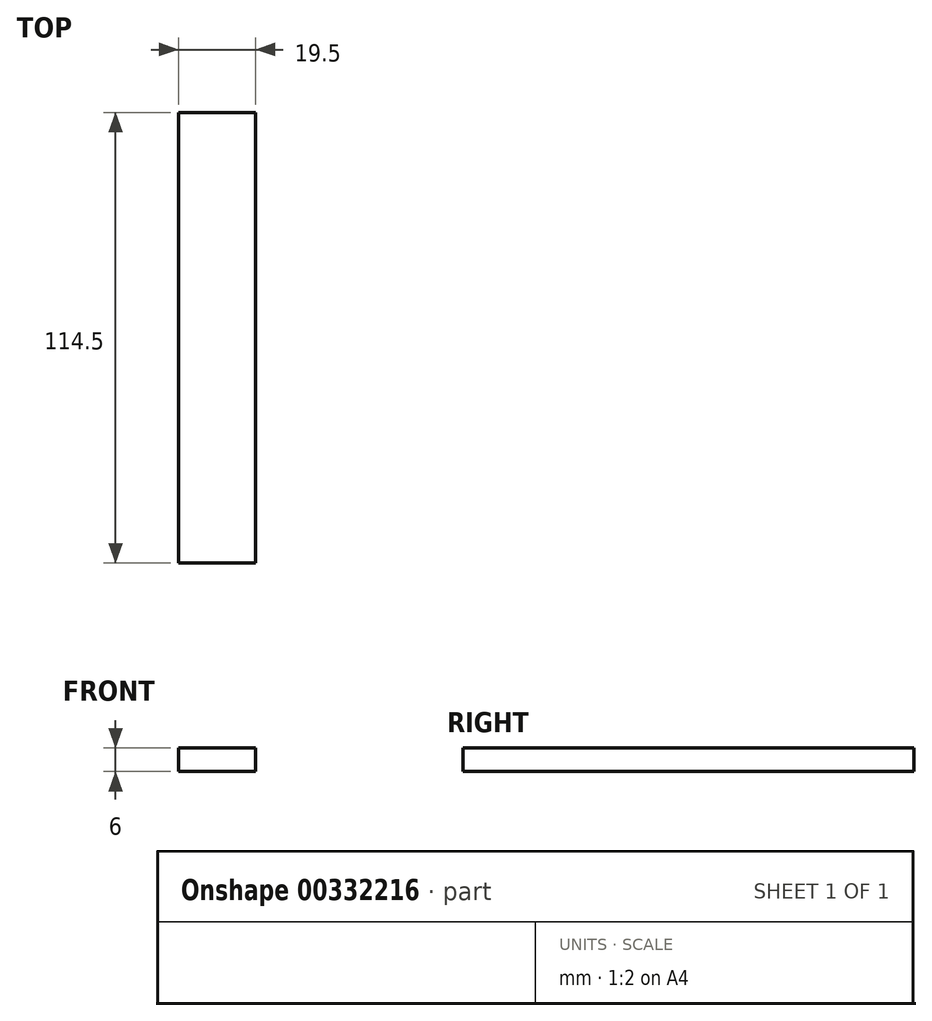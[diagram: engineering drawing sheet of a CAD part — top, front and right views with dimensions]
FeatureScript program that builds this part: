
annotation { "Feature Type Name" : "Feature", "Feature Type Description" : "" }
export const myFeature = defineFeature(function(context is Context, id is Id, definition is map)
    precondition{}
    {
        {
            var Q0;
            Q0=qCreatedBy(makeId("Top.planeOp"),FACE);
            var sketch = newSketch(context, id + "F0", { "sketchPlane" : qUnion([Q0])});
            skLineSegment(sketch, "E0.bottom", {"start": v(-9.75, 57.25) * mm, "end": v(9.75, 57.25) * mm});
            skLineSegment(sketch, "E0.top", {"start": v(-9.75, -57.25) * mm, "end": v(9.75, -57.25) * mm});
            skLineSegment(sketch, "E0.left", {"start": v(-9.75, 57.25) * mm, "end": v(-9.75, -57.25) * mm});
            skLineSegment(sketch, "E0.right", {"start": v(9.75, 57.25) * mm, "end": v(9.75, -57.25) * mm});
            skPoint(sketch, "E0.middle", {"position": v(0, 0) * mm});
            skSolve(sketch);
        }
        {
            var Q0;
            Q0 = qSketchRegion(id + "F0", true);
            extrude(context, id + "F1", {"entities" : qUnion([Q0]), "depth" : 6 * mm});
        }
    });
